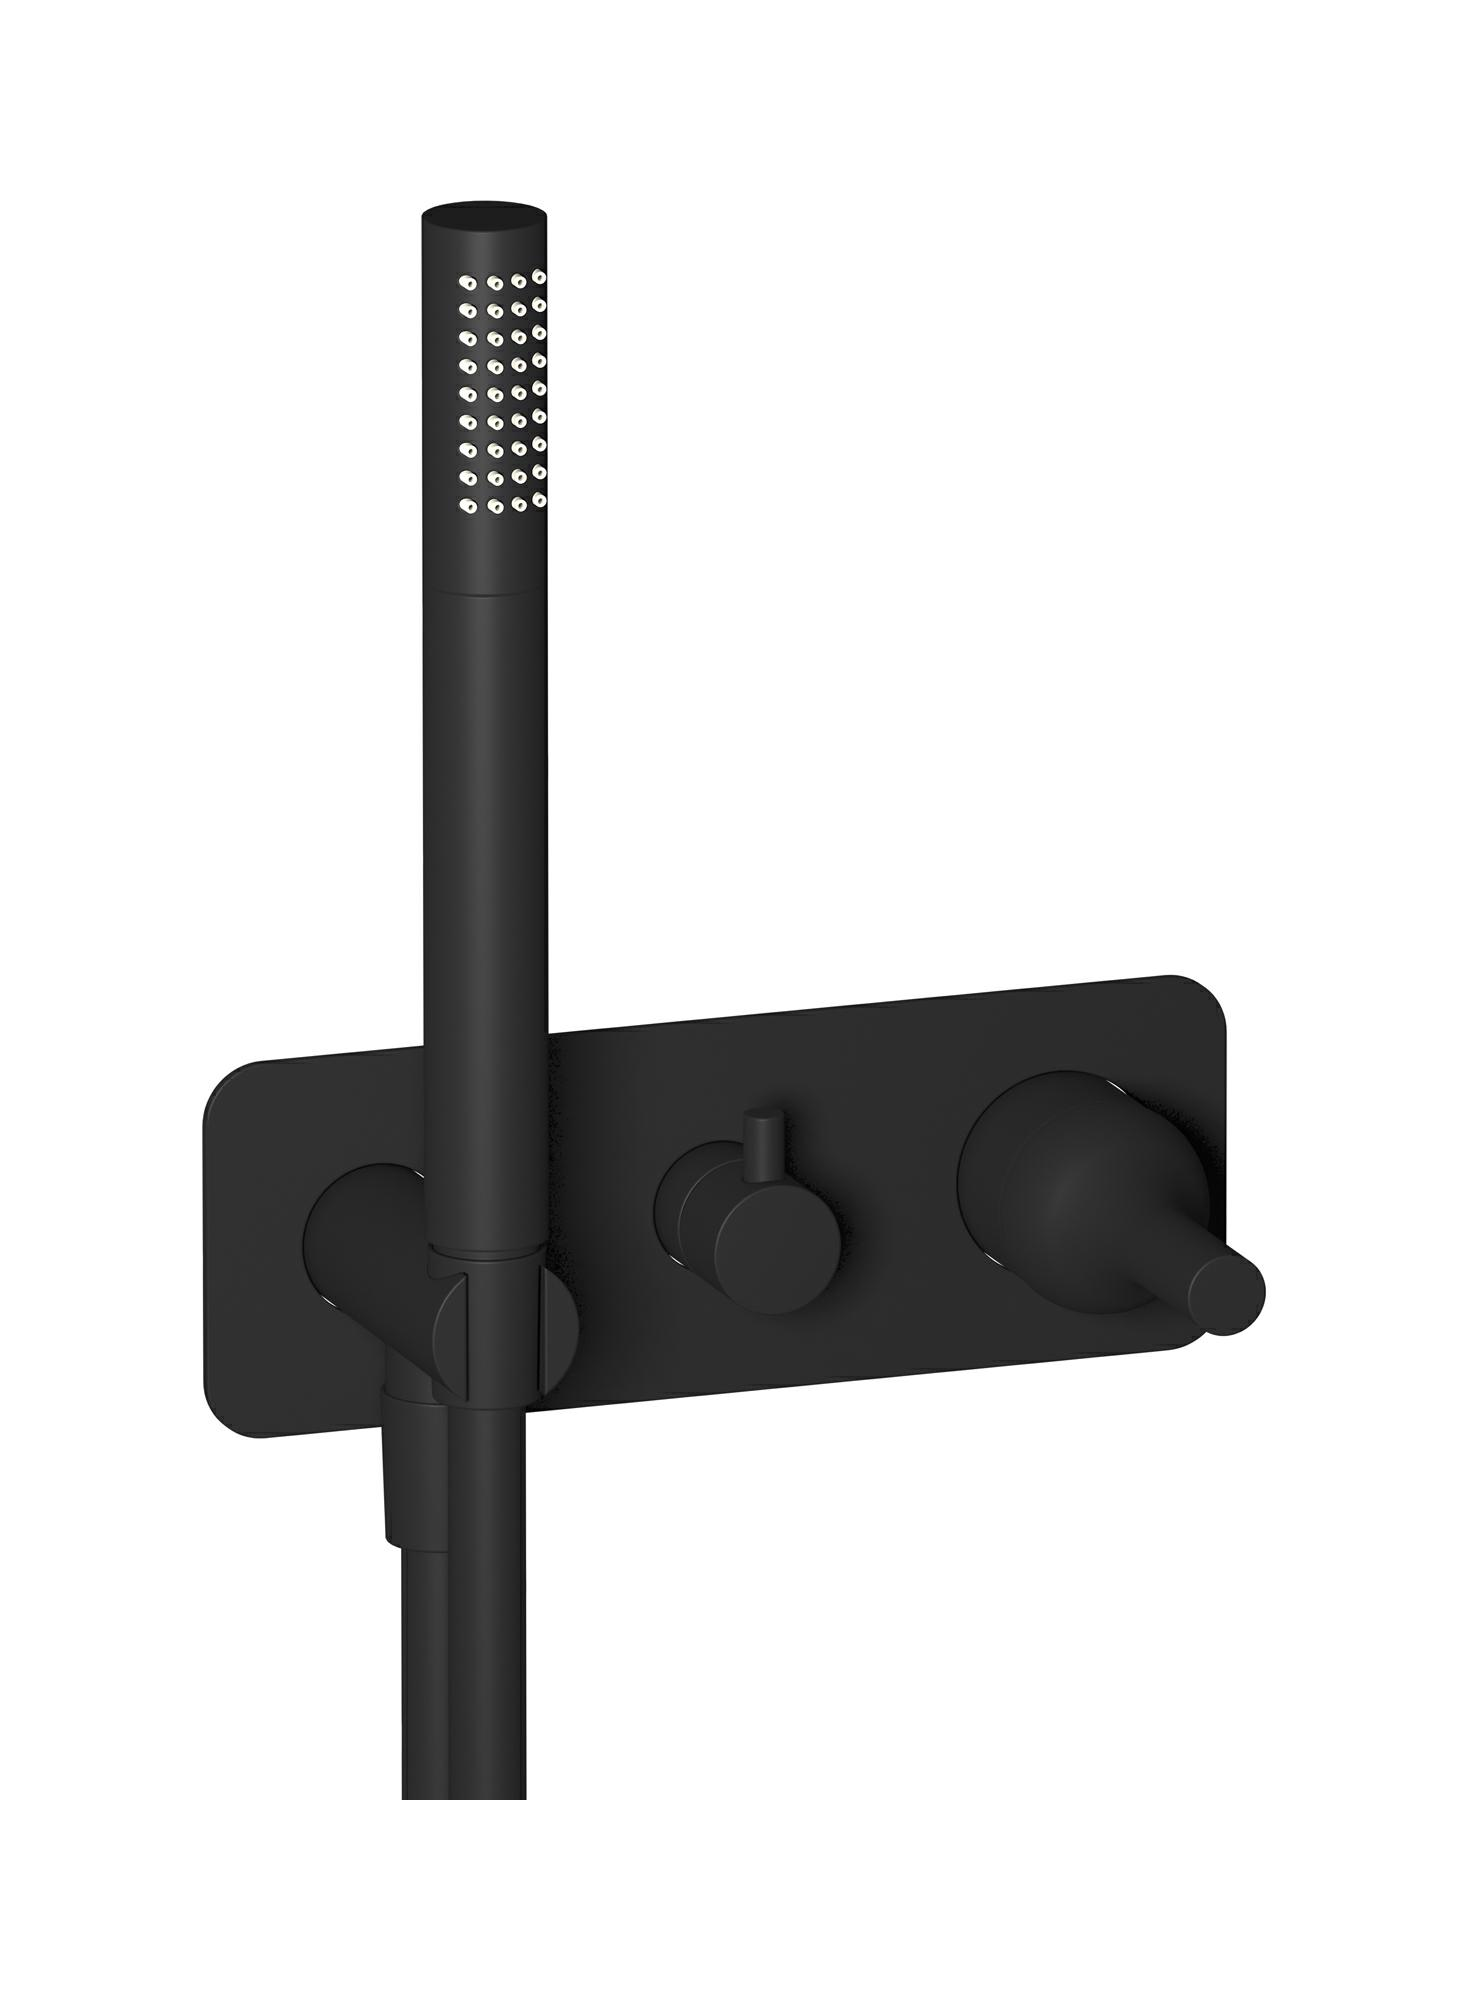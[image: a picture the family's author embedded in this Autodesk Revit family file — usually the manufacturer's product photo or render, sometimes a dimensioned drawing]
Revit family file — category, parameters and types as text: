
# Revit family: BI313
name_source: partatom
category: Apparecchi idraulici
units: mm (PartAtom-declared; Revit-internal decimal feet)

## family parameters
Basato su piano di lavoro = No
Condiviso = No
Mantieni orientamento annotazione = No
Numero OmniClass = 23.45.55.17
Punto di calcolo locali = No
Quota connettore circolare = Usa diametro
Sempre verticale = Sì
Taglio con vuoti quando caricato = No
Tipo di parte = Normale
Titolo OmniClass = Mixing Faucets

## types (4) — shared parameters
Cold water flow = 0,0 L/s
Cold water inlet = 10 mm  [stored 0.0328084 ft]
Commenti sul tipo = Exposed parts for manual wall mixer with two ways diverter and shower kit
Connessione CW = No
Connessione HW = No
Connessione di scarico = No
Connessione di ventilazione = No
Descrizione = Exposed parts for manual wall mixer with two ways diverter and shower kit
Hot water inlet = 10 mm  [stored 0.0328084 ft]
Produttore = IB Rubinetterie S.p.A.
URL = https://www.weareib.it
zero-valued in all types: Prospetto di default

## per-type parameters (varying)
| type | Finishes surface | Immagine tipo | Modello |
| Chrome | IB_Chrome | BI313CC.jpg | BI313CC |
| Brushed nickel | IB_Brushed nickel | BI313SS.jpg | BI313SS |
| Matt white | IB_matt white | BI313BO.jpg | BI313BO |
| Matt black | IB_matt black | BI313NP.jpg | BI313NP |

note: [stored X ft] marks values corroborated as IEEE doubles in the binary element streams (Revit-internal decimal feet)
